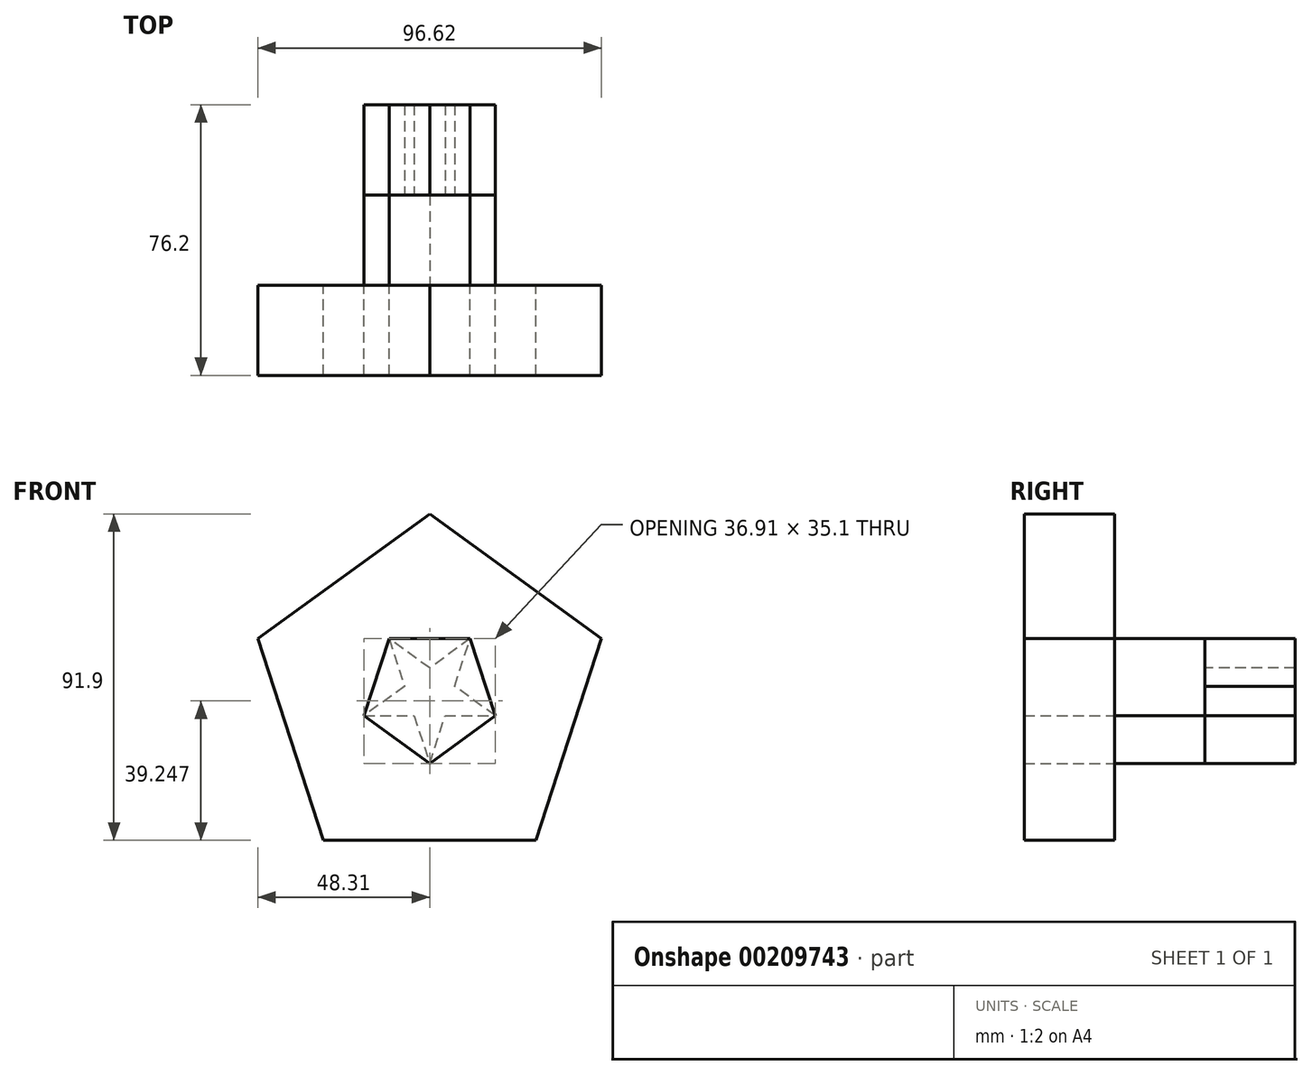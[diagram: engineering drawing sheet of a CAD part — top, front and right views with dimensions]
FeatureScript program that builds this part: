
annotation { "Feature Type Name" : "Feature", "Feature Type Description" : "" }
export const myFeature = defineFeature(function(context is Context, id is Id, definition is map)
    precondition{}
    {
        {
            var Q0;
            Q0=qCreatedBy(makeId("Front.planeOp"),FACE);
            var sketch = newSketch(context, id + "F0", { "sketchPlane" : qUnion([Q0])});
            skCircle(sketch, "E0", {"center": v(0, 0) * mm, "radius": 50.8 * mm});
            skCircle(sketch, "E1.cCircle", {"center": v(0, 0) * mm, "radius": 50.8 * mm, "construction": true});
            skLineSegment(sketch, "E1.0", {"start": v(0, 50.8) * mm, "end": v(48.31, 15.7) * mm});
            skLineSegment(sketch, "E1.1", {"start": v(48.31, 15.7) * mm, "end": v(29.86, -41.1) * mm});
            skLineSegment(sketch, "E1.2", {"start": v(29.86, -41.1) * mm, "end": v(-29.86, -41.1) * mm});
            skLineSegment(sketch, "E1.3", {"start": v(-29.86, -41.1) * mm, "end": v(-48.31, 15.7) * mm});
            skLineSegment(sketch, "E1.4", {"start": v(-48.31, 15.7) * mm, "end": v(0, 50.8) * mm});
            skLineSegment(sketch, "E2", {"start": v(-29.86, -41.1) * mm, "end": v(0, 50.8) * mm});
            skLineSegment(sketch, "E3", {"start": v(-48.31, 15.7) * mm, "end": v(48.31, 15.7) * mm});
            skLineSegment(sketch, "E4", {"start": v(-48.31, 15.7) * mm, "end": v(29.86, -41.1) * mm});
            skLineSegment(sketch, "E5", {"start": v(29.86, -41.1) * mm, "end": v(0, 50.8) * mm});
            skLineSegment(sketch, "E6", {"start": v(48.31, 15.7) * mm, "end": v(-29.86, -41.1) * mm});
            skLineSegment(sketch, "E7", {"start": v(-29.86, -41.1) * mm, "end": v(-18.45, -6) * mm});
            skLineSegment(sketch, "E8", {"start": v(-18.45, -6) * mm, "end": v(-48.31, 15.7) * mm});
            skLineSegment(sketch, "E9", {"start": v(-11.4, 15.7) * mm, "end": v(0, 50.8) * mm});
            skLineSegment(sketch, "E10", {"start": v(11.4, 15.7) * mm, "end": v(48.31, 15.7) * mm});
            skLineSegment(sketch, "E11", {"start": v(18.45, -6) * mm, "end": v(29.86, -41.1) * mm});
            skLineSegment(sketch, "E12", {"start": v(0, -19.4) * mm, "end": v(-29.86, -41.1) * mm});
            skLineSegment(sketch, "E13", {"start": v(0, -19.4) * mm, "end": v(29.86, -41.1) * mm});
            skLineSegment(sketch, "E14", {"start": v(18.45, -6) * mm, "end": v(48.31, 15.7) * mm});
            skLineSegment(sketch, "E15", {"start": v(0, 50.8) * mm, "end": v(11.4, 15.7) * mm});
            skSolve(sketch);
        }
        {
            var Q0;
            Q0=makeQuery(id+"F0.imprint","IMPRINT",FACE,{"disambiguationData":[TD([[makeQuery(id+"F0.imprint","IMPRINT",EDGE,{"derivedFrom":sQuery(id+"F0.wireOp",EDGE,"E4")}),-1.0]])]});
            var Q1;
            {var subQ0=sQuery(id+"F0.wireOp",EDGE,"E2");Q1=makeQuery(id+"F0.imprint","IMPRINT",FACE,{"disambiguationData":[TD([[makeQuery(id+"F0.imprint","IMPRINT",EDGE,{"derivedFrom":subQ0}),1.0]])]});}
            var Q2;
            {var subQ2=sQuery(id+"F0.wireOp",EDGE,"E2");Q2=makeQuery(id+"F0.imprint","IMPRINT",FACE,{"disambiguationData":[TD([[makeQuery(id+"F0.imprint","IMPRINT",EDGE,{"derivedFrom":subQ2}),-1.0]])]});}
            var Q3;
            {var subQ0=sQuery(id+"F0.wireOp",EDGE,"E9");Q3=makeQuery(id+"F0.imprint","IMPRINT",FACE,{"disambiguationData":[TD([[makeQuery(id+"F0.imprint","IMPRINT",EDGE,{"derivedFrom":subQ0}),-1.0]])]});}
            var Q4;
            Q4=makeQuery(id+"F0.imprint","IMPRINT",FACE,{"disambiguationData":[TD([[makeQuery(id+"F0.imprint","IMPRINT",EDGE,{"derivedFrom":sQuery(id+"F0.wireOp",EDGE,"E5")}),-1.0]])]});
            var Q5;
            Q5=makeQuery(id+"F0.imprint","IMPRINT",FACE,{"disambiguationData":[TD([[makeQuery(id+"F0.imprint","IMPRINT",EDGE,{"derivedFrom":sQuery(id+"F0.wireOp",EDGE,"E6")}),1.0]])]});
            extrude(context, id + "F1", {"entities" : qUnion([Q0, Q1, Q2, Q3, Q4, Q5]), "depth" : 25.4 * mm});
        }
        {
            var Q0;
            Q0=makeQuery(id+"F1.opExtrude","CAP_FACE",FACE,{"disambiguationData":[OSD([sQuery(id+"F0.wireOp",EDGE,"E3"),sQuery(id+"F0.wireOp",EDGE,"E7"),sQuery(id+"F0.wireOp",EDGE,"E8"),sQuery(id+"F0.wireOp",EDGE,"E9"),sQuery(id+"F0.wireOp",EDGE,"E10"),sQuery(id+"F0.wireOp",EDGE,"E11"),sQuery(id+"F0.wireOp",EDGE,"E12"),sQuery(id+"F0.wireOp",EDGE,"E13"),sQuery(id+"F0.wireOp",EDGE,"E14"),sQuery(id+"F0.wireOp",EDGE,"E15")])],"isStart":true});
            var sketch = newSketch(context, id + "F2", { "sketchPlane" : qUnion([Q0])});
            skLineSegment(sketch, "E16", {"start": v(-18.45, -6) * mm, "end": v(-11.4, 15.7) * mm});
            skLineSegment(sketch, "E17", {"start": v(-11.4, 15.7) * mm, "end": v(11.4, 15.7) * mm});
            skLineSegment(sketch, "E18", {"start": v(11.4, 15.7) * mm, "end": v(18.45, -6) * mm});
            skLineSegment(sketch, "E19", {"start": v(18.45, -6) * mm, "end": v(0, -19.4) * mm});
            skLineSegment(sketch, "E20", {"start": v(0, -19.4) * mm, "end": v(-18.45, -6) * mm});
            skSolve(sketch);
        }
        {
            var Q0;
            Q0=makeQuery(id+"F2.imprint","IMPRINT",FACE,{"disambiguationData":[TD([[makeQuery(id+"F2.imprint","IMPRINT",EDGE,{"derivedFrom":sQuery(id+"F2.wireOp",EDGE,"E16")}),-1.0]])]});
            extrude(context, id + "F3", {"entities" : qUnion([Q0]), "operationType" : NewBodyOperationType.ADD, "depth" : 25.4 * mm});
        }
        {
            var Q0;
            Q0=makeQuery(id+"F3.opExtrude","CAP_FACE",FACE,{"disambiguationData":[OSD([sQuery(id+"F2.wireOp",EDGE,"E16"),sQuery(id+"F2.wireOp",EDGE,"E17"),sQuery(id+"F2.wireOp",EDGE,"E18"),sQuery(id+"F2.wireOp",EDGE,"E19"),sQuery(id+"F2.wireOp",EDGE,"E20")])],"isStart":false});
            var sketch = newSketch(context, id + "F4", { "sketchPlane" : qUnion([Q0])});
            skLineSegment(sketch, "E21", {"start": v(-18.45, -6) * mm, "end": v(11.4, 15.7) * mm});
            skLineSegment(sketch, "E22", {"start": v(11.4, 15.7) * mm, "end": v(0, -19.4) * mm});
            skLineSegment(sketch, "E23", {"start": v(0, -19.4) * mm, "end": v(-11.4, 15.7) * mm});
            skLineSegment(sketch, "E24", {"start": v(-11.4, 15.7) * mm, "end": v(18.45, -6) * mm});
            skLineSegment(sketch, "E25", {"start": v(18.45, -6) * mm, "end": v(-18.45, -6) * mm});
            skSolve(sketch);
        }
        {
            var Q0;
            {var subQ0=sQuery(id+"F4.wireOp",EDGE,"E24");var subQ1=sQuery(id+"F4.wireOp",EDGE,"E22");var subQ2=makeQuery(id+"F4.imprint","INTERSECT",VERTEX,{"derivedFrom":[subQ1,subQ0]});Q0=makeQuery(id+"F4.imprint","IMPRINT",FACE,{"disambiguationData":[TD([[makeQuery(id+"F4.imprint","IMPRINT",EDGE,{"disambiguationData":[TD([[subQ2,-1.0]])],"derivedFrom":subQ1}),1.0]])]});}
            var Q1;
            {var subQ1=sQuery(id+"F4.wireOp",EDGE,"E21");var subQ3=sQuery(id+"F4.wireOp",EDGE,"E24");var subQ4=makeQuery(id+"F4.imprint","INTERSECT",VERTEX,{"derivedFrom":[subQ1,subQ3]});Q1=makeQuery(id+"F4.imprint","IMPRINT",FACE,{"disambiguationData":[TD([[makeQuery(id+"F4.imprint","IMPRINT",EDGE,{"disambiguationData":[TD([[subQ4,-1.0]])],"derivedFrom":subQ3}),1.0]])]});}
            var Q2;
            {var subQ1=sQuery(id+"F4.wireOp",EDGE,"E21");var subQ7=sQuery(id+"F4.wireOp",EDGE,"E23");var subQ8=makeQuery(id+"F4.imprint","INTERSECT",VERTEX,{"derivedFrom":[subQ1,subQ7]});Q2=makeQuery(id+"F4.imprint","IMPRINT",FACE,{"disambiguationData":[TD([[makeQuery(id+"F4.imprint","IMPRINT",EDGE,{"disambiguationData":[TD([[subQ8,-1.0]])],"derivedFrom":subQ1}),-1.0]])]});}
            var Q3;
            {var subQ0=sQuery(id+"F4.wireOp",EDGE,"E23");var subQ1=sQuery(id+"F4.wireOp",EDGE,"E21");var subQ2=makeQuery(id+"F4.imprint","INTERSECT",VERTEX,{"derivedFrom":[subQ1,subQ0]});Q3=makeQuery(id+"F4.imprint","IMPRINT",FACE,{"disambiguationData":[TD([[makeQuery(id+"F4.imprint","IMPRINT",EDGE,{"disambiguationData":[TD([[subQ2,-1.0]])],"derivedFrom":subQ1}),1.0]])]});}
            var Q4;
            {var subQ1=sQuery(id+"F4.wireOp",EDGE,"E21");var subQ3=sQuery(id+"F4.wireOp",EDGE,"E23");var subQ4=makeQuery(id+"F4.imprint","INTERSECT",VERTEX,{"derivedFrom":[subQ1,subQ3]});Q4=makeQuery(id+"F4.imprint","IMPRINT",FACE,{"disambiguationData":[TD([[makeQuery(id+"F4.imprint","IMPRINT",EDGE,{"disambiguationData":[TD([[subQ4,1.0]])],"derivedFrom":subQ3}),1.0]])]});}
            var Q5;
            {var subQ1=sQuery(id+"F4.wireOp",EDGE,"E22");var subQ3=sQuery(id+"F4.wireOp",EDGE,"E25");var subQ4=makeQuery(id+"F4.imprint","INTERSECT",VERTEX,{"derivedFrom":[subQ1,subQ3]});Q5=makeQuery(id+"F4.imprint","IMPRINT",FACE,{"disambiguationData":[TD([[makeQuery(id+"F4.imprint","IMPRINT",EDGE,{"disambiguationData":[TD([[subQ4,-1.0]])],"derivedFrom":subQ3}),1.0]])]});}
            extrude(context, id + "F5", {"entities" : qUnion([Q0, Q1, Q2, Q3, Q4, Q5]), "operationType" : NewBodyOperationType.ADD, "depth" : 25.4 * mm});
        }
    });
